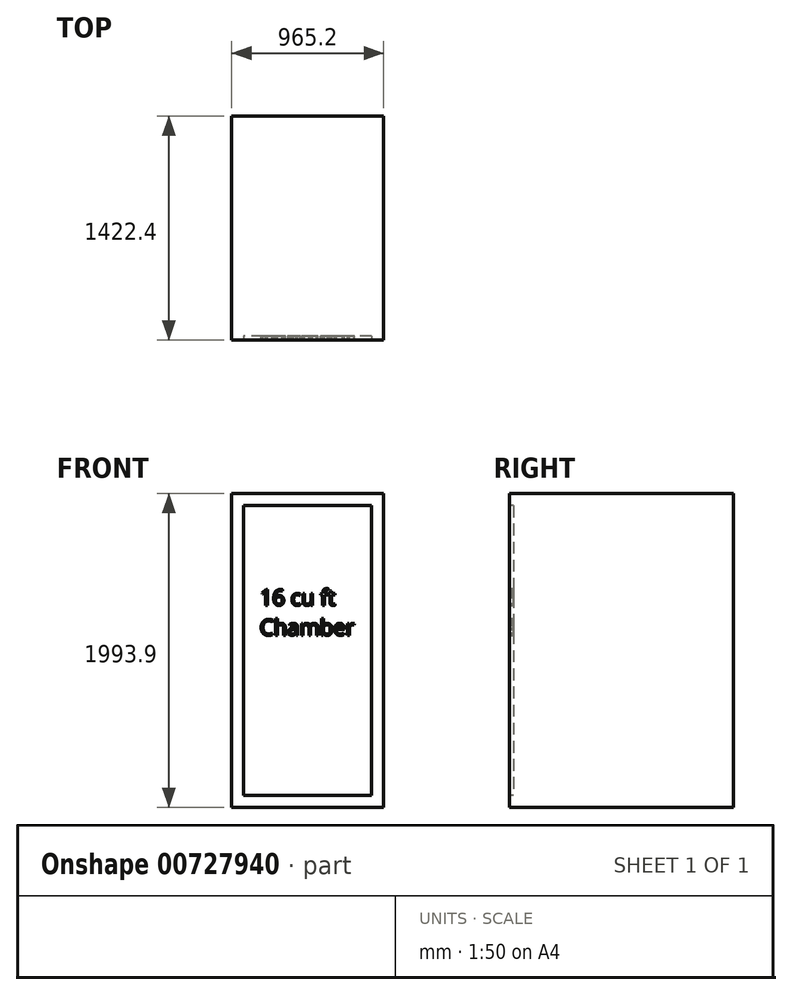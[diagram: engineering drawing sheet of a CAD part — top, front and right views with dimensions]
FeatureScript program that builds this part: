
annotation { "Feature Type Name" : "Feature", "Feature Type Description" : "" }
export const myFeature = defineFeature(function(context is Context, id is Id, definition is map)
    precondition{}
    {
        {
            var Q0;
            Q0=qCreatedBy(makeId("Top.planeOp"),FACE);
            var sketch = newSketch(context, id + "F0", { "sketchPlane" : qUnion([Q0])});
            skLineSegment(sketch, "E0.bottom", {"start": v(482.6, -711.2) * mm, "end": v(-482.6, -711.2) * mm});
            skLineSegment(sketch, "E0.top", {"start": v(482.6, 711.2) * mm, "end": v(-482.6, 711.2) * mm});
            skLineSegment(sketch, "E0.left", {"start": v(482.6, -711.2) * mm, "end": v(482.6, 711.2) * mm});
            skLineSegment(sketch, "E0.right", {"start": v(-482.6, -711.2) * mm, "end": v(-482.6, 711.2) * mm});
            skPoint(sketch, "E0.middle", {"position": v(0, 0) * mm});
            skSolve(sketch);
        }
        {
            var Q0;
            Q0 = qSketchRegion(id + "F0", true);
            extrude(context, id + "F1", {"entities" : qUnion([Q0]), "depth" : 1993.9 * mm, "offsetDistance" : 25.4 * mm});
        }
        {
            var Q0;
            Q0=makeQuery(id+"F1.opExtrude","SWEPT_FACE",FACE,{"disambiguationData":[OSD([sQuery(id+"F0.wireOp",EDGE,"E0.bottom")])]});
            var sketch = newSketch(context, id + "F2", { "sketchPlane" : qUnion([Q0])});
            skLineSegment(sketch, "E1.0", {"start": v(406.4, 1917.7) * mm, "end": v(-406.4, 1917.7) * mm});
            skLineSegment(sketch, "E1.1", {"start": v(406.4, 1917.7) * mm, "end": v(406.4, 76.2) * mm});
            skLineSegment(sketch, "E1.2", {"start": v(406.4, 76.2) * mm, "end": v(-406.4, 76.2) * mm});
            skLineSegment(sketch, "E1.3", {"start": v(-406.4, 1917.7) * mm, "end": v(-406.4, 76.2) * mm});
            skSolve(sketch);
        }
        {
            var Q0;
            Q0 = qSketchRegion(id + "F2", true);
            extrude(context, id + "F3", {"entities" : qUnion([Q0]), "operationType" : NewBodyOperationType.REMOVE, "oppositeDirection" : true, "depth" : 25.4 * mm, "offsetDistance" : 25.4 * mm});
        }
        {
            var Q0;
            Q0=makeQuery(id+"F3.boolean.opBoolean","COPY",FACE,{"derivedFrom":makeQuery(id+"F3.opExtrude","CAP_FACE",FACE,{"disambiguationData":[OSD([sQuery(id+"F2.wireOp",EDGE,"E1.0"),sQuery(id+"F2.wireOp",EDGE,"E1.1"),sQuery(id+"F2.wireOp",EDGE,"E1.2"),sQuery(id+"F2.wireOp",EDGE,"E1.3")])],"isStart":false})});
            var sketch = newSketch(context, id + "F4", { "sketchPlane" : qUnion([Q0])});
            skText(sketch, "E2", { "text": "16 cu ft\nChamber", "fontName": "OpenSans-Regular.ttf"});
            const initialGuessF4  = {"E2": [-0.3048, 1.28372, 1, 0, 0.10058]};
            skSetInitialGuess(sketch, initialGuessF4);
            skSolve(sketch);
        }
        {
            var Q0;
            Q0 = qSketchRegion(id + "F4", true);
            extrude(context, id + "F5", {"entities" : qUnion([Q0]), "operationType" : NewBodyOperationType.ADD, "depth" : 25.4 * mm, "offsetDistance" : 25.4 * mm});
        }
    });
